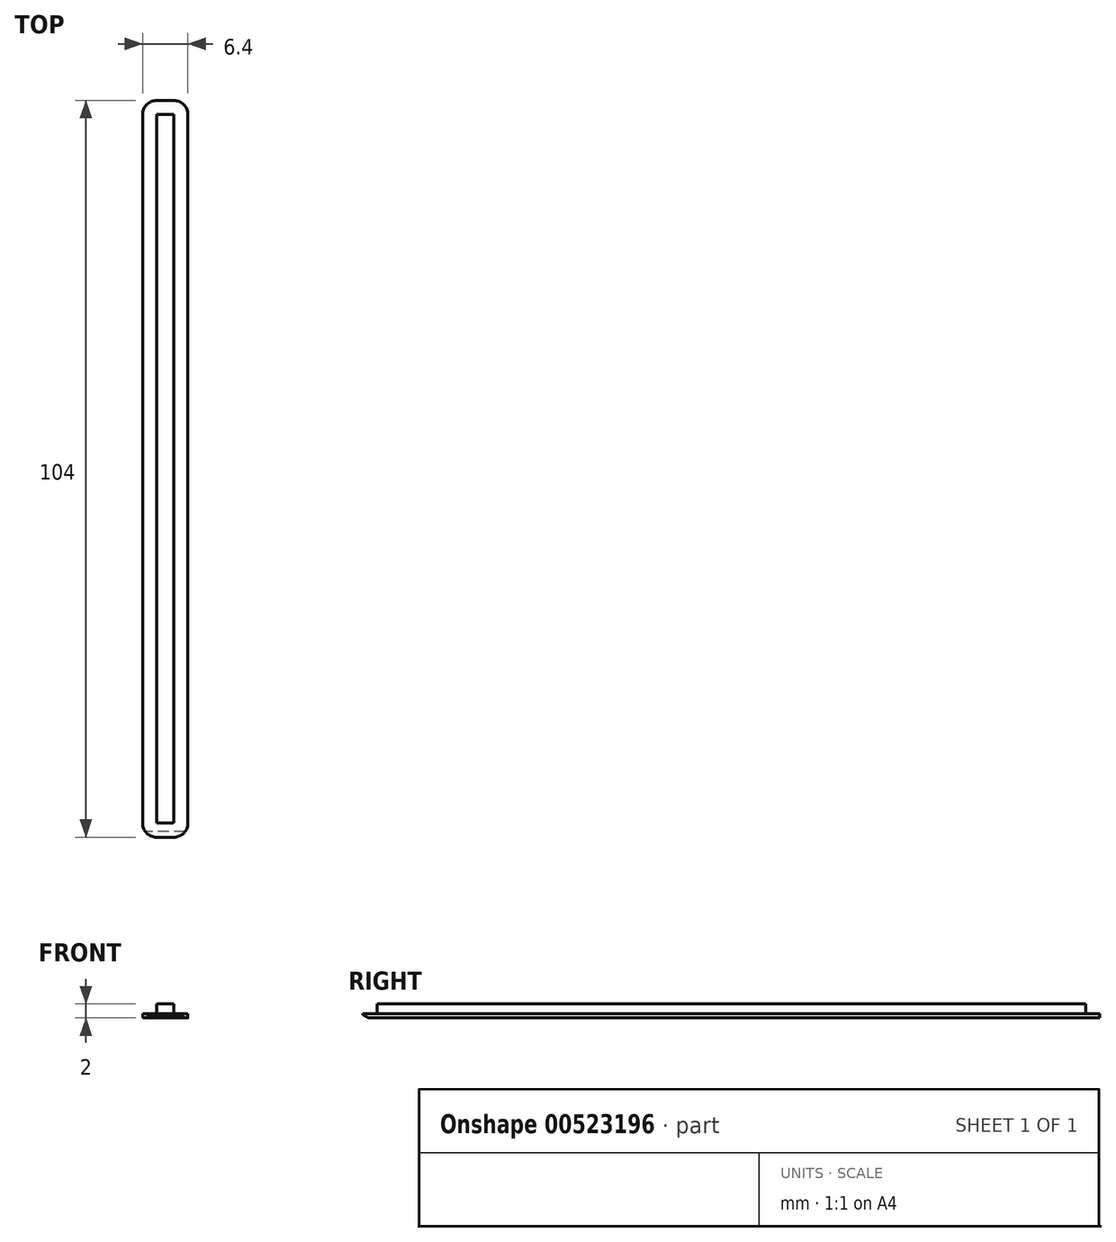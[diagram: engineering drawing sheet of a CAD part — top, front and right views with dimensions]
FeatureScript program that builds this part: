
annotation { "Feature Type Name" : "Feature", "Feature Type Description" : "" }
export const myFeature = defineFeature(function(context is Context, id is Id, definition is map)
    precondition{}
    {
        {
            var Q0;
            Q0=qCreatedBy(makeId("Top.planeOp"),FACE);
            var sketch = newSketch(context, id + "F0", { "sketchPlane" : qUnion([Q0])});
            skLineSegment(sketch, "E0.bottom", {"start": v(1.2, -50) * mm, "end": v(-1.2, -50) * mm});
            skLineSegment(sketch, "E0.top", {"start": v(1.2, 50) * mm, "end": v(-1.2, 50) * mm});
            skLineSegment(sketch, "E0.left", {"start": v(1.2, -50) * mm, "end": v(1.2, 50) * mm});
            skLineSegment(sketch, "E0.right", {"start": v(-1.2, -50) * mm, "end": v(-1.2, 50) * mm});
            skPoint(sketch, "E0.middle", {"position": v(0, 0) * mm});
            skLineSegment(sketch, "E1.0", {"start": v(-3.2, -52) * mm, "end": v(-3.2, 52) * mm});
            skLineSegment(sketch, "E1.1", {"start": v(3.2, -52) * mm, "end": v(-3.2, -52) * mm});
            skLineSegment(sketch, "E1.2", {"start": v(3.2, -52) * mm, "end": v(3.2, 52) * mm});
            skLineSegment(sketch, "E1.3", {"start": v(3.2, 52) * mm, "end": v(-3.2, 52) * mm});
            skSolve(sketch);
        }
        {
            var Q0;
            Q0 = qSketchRegion(id + "F0", true);
            extrude(context, id + "F1", {"entities" : qUnion([Q0]), "depth" : (.2 * 3) * mm, "offsetDistance" : 25 * mm});
        }
        {
            var Q0;
            Q0=makeQuery(id+"F0.imprint","IMPRINT",FACE,{"disambiguationData":[TD([[makeQuery(id+"F0.imprint","IMPRINT",EDGE,{"derivedFrom":sQuery(id+"F0.wireOp",EDGE,"E0.bottom")}),-1.0]])]});
            extrude(context, id + "F2", {"entities" : qUnion([Q0]), "operationType" : NewBodyOperationType.ADD, "depth" : (.2 * 10) * mm, "offsetDistance" : 25 * mm});
        }
        {
            var Q0;
            Q0=makeQuery(id+"F1.opExtrude","SWEPT_EDGE",EDGE,{"disambiguationData":[OSD([sQuery(id+"F0.wireOp",EDGE,"E1.0"),sQuery(id+"F0.wireOp",EDGE,"E1.1")])]});
            var Q1;
            Q1=makeQuery(id+"F1.opExtrude","SWEPT_EDGE",EDGE,{"disambiguationData":[OSD([sQuery(id+"F0.wireOp",EDGE,"E1.0"),sQuery(id+"F0.wireOp",EDGE,"E1.3")])]});
            var Q2;
            Q2=makeQuery(id+"F1.opExtrude","SWEPT_EDGE",EDGE,{"disambiguationData":[OSD([sQuery(id+"F0.wireOp",EDGE,"E1.2"),sQuery(id+"F0.wireOp",EDGE,"E1.3")])]});
            var Q3;
            Q3=makeQuery(id+"F1.opExtrude","SWEPT_EDGE",EDGE,{"disambiguationData":[OSD([sQuery(id+"F0.wireOp",EDGE,"E1.1"),sQuery(id+"F0.wireOp",EDGE,"E1.2")])]});
            fillet(context, id + "F3", {"entities" : qUnion([Q0, Q1, Q2, Q3]), "radius" : 2 * mm, "tangentPropagation" : true, "allowEdgeOverflow" : false});
        }
        {
            var Q0;
            Q0=makeQuery(id+"F1.opExtrude","CAP_EDGE",EDGE,{"disambiguationData":[OSD([sQuery(id+"F0.wireOp",EDGE,"E1.1")])],"isStart":true});
            chamfer(context, id + "F4", {"entities" : qUnion([Q0]), "chamferType" : ChamferType.OFFSET_ANGLE, "width" : .8 * mm, "oppositeDirection" : false, "angle" : 30 * degree});
        }
    });
